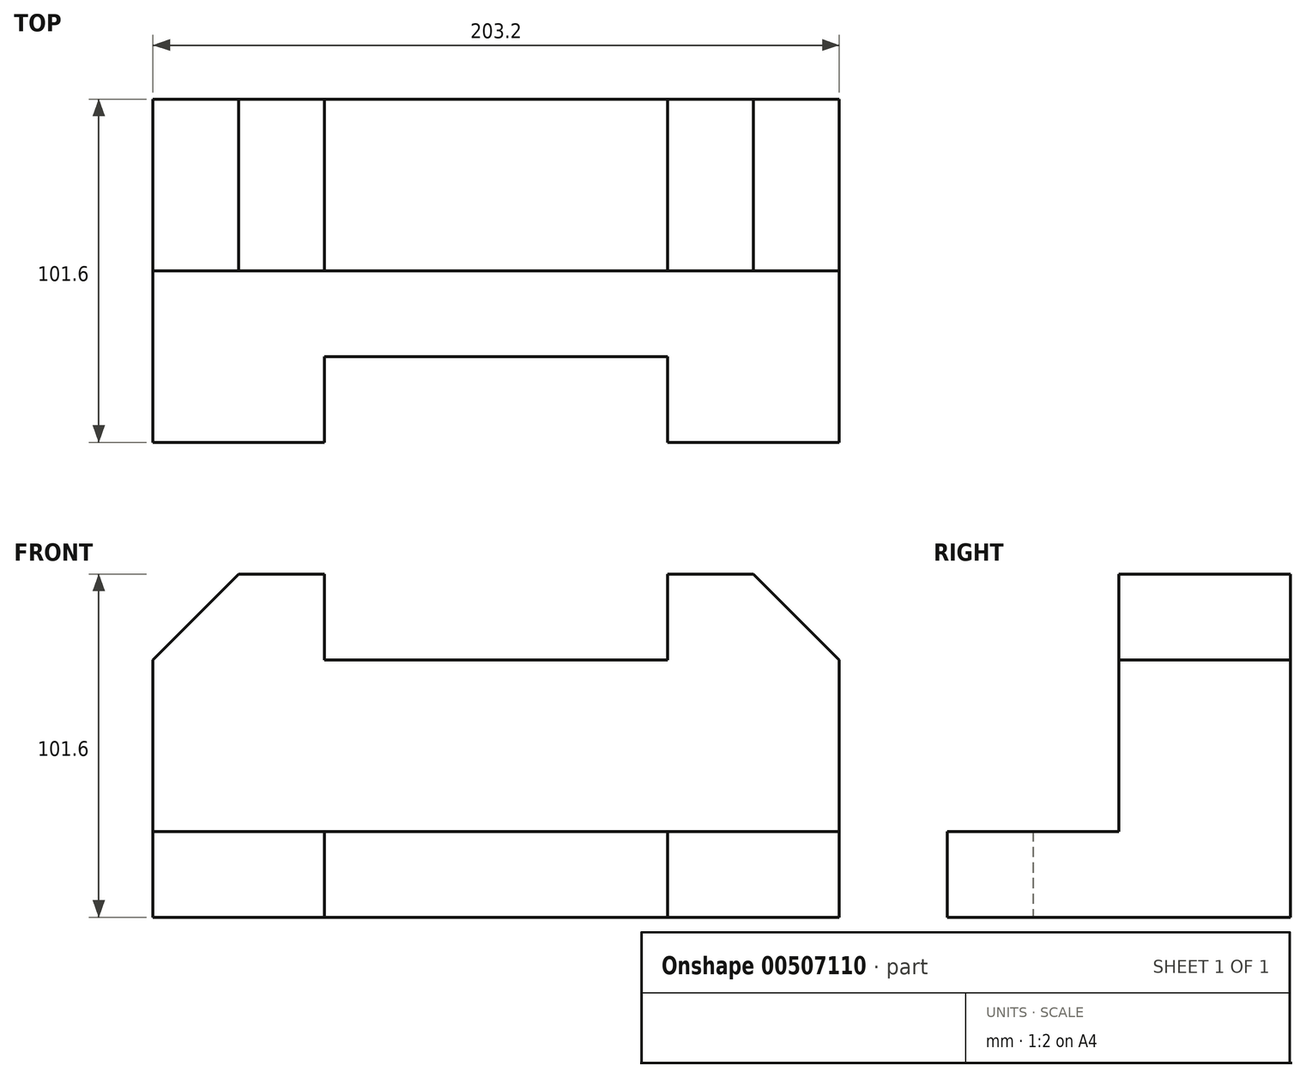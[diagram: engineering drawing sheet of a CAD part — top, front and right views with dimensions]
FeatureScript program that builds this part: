
annotation { "Feature Type Name" : "Feature", "Feature Type Description" : "" }
export const myFeature = defineFeature(function(context is Context, id is Id, definition is map)
    precondition{}
    {
        {
            var Q0;
            Q0=qCreatedBy(makeId("Top.planeOp"),FACE);
            var sketch = newSketch(context, id + "F0", { "sketchPlane" : qUnion([Q0])});
            skLineSegment(sketch, "E0", {"start": v(0, 0) * mm, "end": v(-50.8, 0) * mm});
            skLineSegment(sketch, "E1", {"start": v(-50.8, 0) * mm, "end": v(-50.8, 25.4) * mm});
            skLineSegment(sketch, "E2", {"start": v(-50.8, 25.4) * mm, "end": v(-152.4, 25.4) * mm});
            skLineSegment(sketch, "E3", {"start": v(-152.4, 25.4) * mm, "end": v(-152.4, 0) * mm});
            skLineSegment(sketch, "E4", {"start": v(-152.4, 0) * mm, "end": v(-203.2, 0) * mm});
            skLineSegment(sketch, "E5", {"start": v(-203.2, 0) * mm, "end": v(-203.2, 101.6) * mm});
            skLineSegment(sketch, "E6", {"start": v(-203.2, 101.6) * mm, "end": v(0, 101.6) * mm});
            skLineSegment(sketch, "E7", {"start": v(0, 101.6) * mm, "end": v(0, 0) * mm});
            skSolve(sketch);
        }
        {
            var Q0;
            Q0=makeQuery(id+"F0.imprint","IMPRINT",FACE,{"disambiguationData":[TD([[makeQuery(id+"F0.imprint","IMPRINT",EDGE,{"derivedFrom":sQuery(id+"F0.wireOp",EDGE,"E0")}),-1.0]])]});
            extrude(context, id + "F1", {"entities" : qUnion([Q0]), "depth" : 25.4 * mm});
        }
        {
            var Q0;
            Q0=makeQuery(id+"F1.opExtrude","CAP_FACE",FACE,{"disambiguationData":[OSD([sQuery(id+"F0.wireOp",EDGE,"E0"),sQuery(id+"F0.wireOp",EDGE,"E1"),sQuery(id+"F0.wireOp",EDGE,"E2"),sQuery(id+"F0.wireOp",EDGE,"E3"),sQuery(id+"F0.wireOp",EDGE,"E4"),sQuery(id+"F0.wireOp",EDGE,"E5"),sQuery(id+"F0.wireOp",EDGE,"E6"),sQuery(id+"F0.wireOp",EDGE,"E7")])],"isStart":false});
            var sketch = newSketch(context, id + "F2", { "sketchPlane" : qUnion([Q0])});
            skLineSegment(sketch, "E8", {"start": v(0, 101.6) * mm, "end": v(0, 50.8) * mm});
            skLineSegment(sketch, "E9", {"start": v(0, 50.8) * mm, "end": v(-203.2, 50.8) * mm});
            skLineSegment(sketch, "E10", {"start": v(-203.2, 50.8) * mm, "end": v(-203.2, 101.6) * mm});
            skLineSegment(sketch, "E11", {"start": v(-203.2, 101.6) * mm, "end": v(0, 101.6) * mm});
            skSolve(sketch);
        }
        {
            var Q0;
            Q0=makeQuery(id+"F2.imprint","IMPRINT",FACE,{"disambiguationData":[TD([[makeQuery(id+"F2.imprint","IMPRINT",EDGE,{"derivedFrom":sQuery(id+"F2.wireOp",EDGE,"E8")}),-1.0]])]});
            extrude(context, id + "F3", {"entities" : qUnion([Q0]), "operationType" : NewBodyOperationType.ADD, "depth" : 50.8 * mm});
        }
        {
            var Q0;
            Q0=makeQuery(id+"F3.opExtrude","SWEPT_FACE",FACE,{"disambiguationData":[OSD([sQuery(id+"F2.wireOp",EDGE,"E9")])]});
            var sketch = newSketch(context, id + "F4", { "sketchPlane" : qUnion([Q0])});
            skLineSegment(sketch, "E12", {"start": v(0, 76.2) * mm, "end": v(-50.8, 76.2) * mm});
            skLineSegment(sketch, "E13", {"start": v(-50.8, 76.2) * mm, "end": v(-50.8, 101.6) * mm});
            skLineSegment(sketch, "E14", {"start": v(-50.8, 101.6) * mm, "end": v(-25.4, 101.6) * mm});
            skLineSegment(sketch, "E15", {"start": v(-25.4, 101.6) * mm, "end": v(0, 76.2) * mm});
            skLineSegment(sketch, "E16", {"start": v(-203.2, 76.2) * mm, "end": v(-152.4, 76.2) * mm});
            skLineSegment(sketch, "E17", {"start": v(-152.4, 76.2) * mm, "end": v(-152.4, 101.6) * mm});
            skLineSegment(sketch, "E18", {"start": v(-152.4, 101.6) * mm, "end": v(-177.8, 101.6) * mm});
            skLineSegment(sketch, "E19", {"start": v(-177.8, 101.6) * mm, "end": v(-203.2, 76.2) * mm});
            skSolve(sketch);
        }
        {
            var Q0;
            Q0=makeQuery(id+"F4.imprint","IMPRINT",FACE,{"disambiguationData":[TD([[makeQuery(id+"F4.imprint","IMPRINT",EDGE,{"derivedFrom":sQuery(id+"F4.wireOp",EDGE,"E16")}),-1.0]])]});
            var Q1;
            Q1=makeQuery(id+"F4.imprint","IMPRINT",FACE,{"disambiguationData":[TD([[makeQuery(id+"F4.imprint","IMPRINT",EDGE,{"derivedFrom":sQuery(id+"F4.wireOp",EDGE,"E12")}),-1.0]])]});
            extrude(context, id + "F5", {"entities" : qUnion([Q0, Q1]), "operationType" : NewBodyOperationType.ADD, "oppositeDirection" : true, "depth" : 50.8 * mm});
        }
    });
